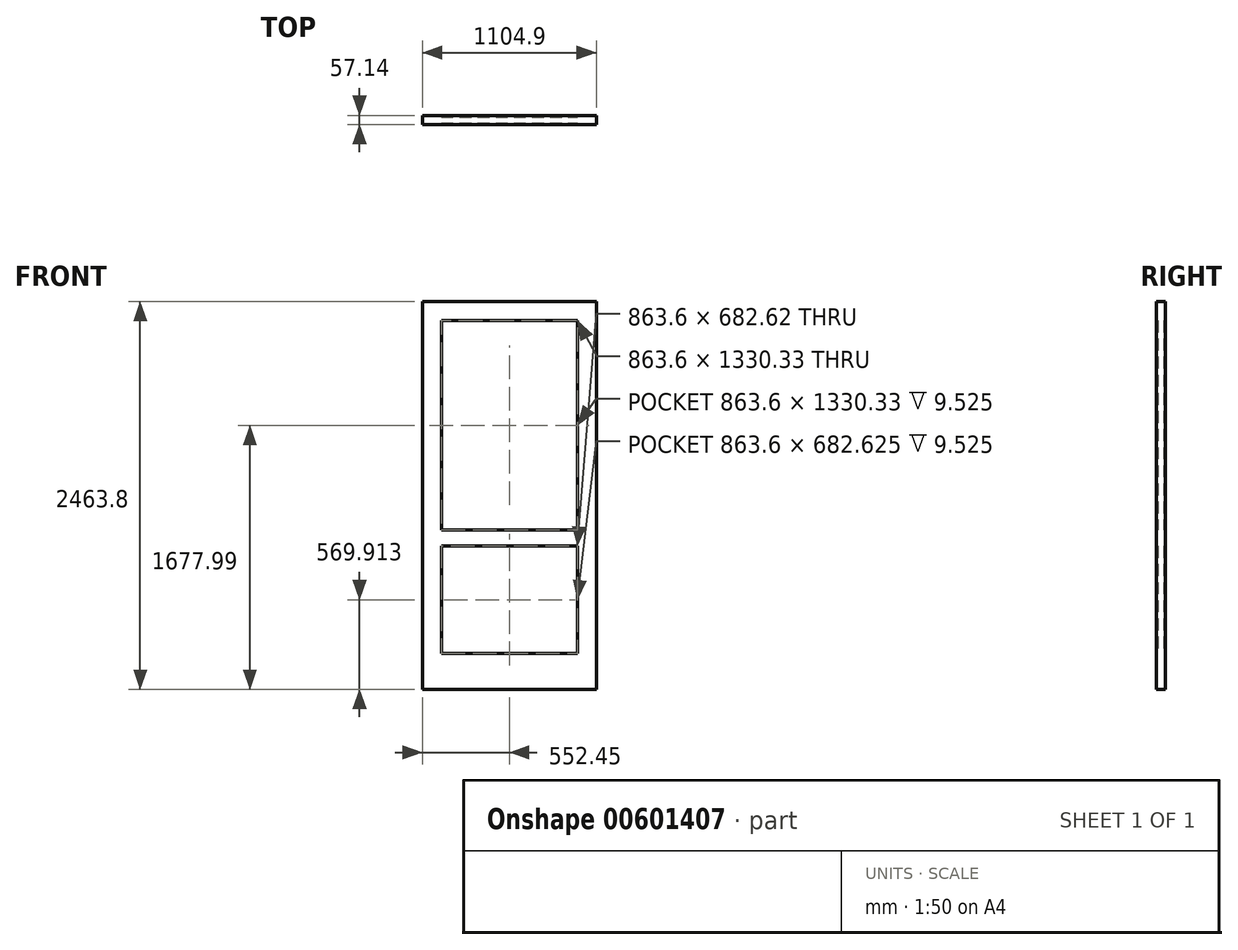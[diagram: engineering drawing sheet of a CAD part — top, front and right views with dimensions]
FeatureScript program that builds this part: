
annotation { "Feature Type Name" : "Feature", "Feature Type Description" : "" }
export const myFeature = defineFeature(function(context is Context, id is Id, definition is map)
    precondition{}
    {
        {
            var Q0;
            Q0=qCreatedBy(makeId("Front.planeOp"),FACE);
            var sketch = newSketch(context, id + "F0", { "sketchPlane" : qUnion([Q0])});
            skLineSegment(sketch, "E0.bottom", {"start": v(0, 0) * mm, "end": v(-1104.9, 0) * mm});
            skLineSegment(sketch, "E0.top", {"start": v(0, 2463.8) * mm, "end": v(-1104.9, 2463.8) * mm});
            skLineSegment(sketch, "E0.left", {"start": v(0, 0) * mm, "end": v(0, 2463.8) * mm});
            skLineSegment(sketch, "E0.right", {"start": v(-1104.9, 0) * mm, "end": v(-1104.9, 2463.8) * mm});
            skLineSegment(sketch, "E1.bottom", {"start": v(-984.25, 2343.15) * mm, "end": v(-120.65, 2343.15) * mm});
            skLineSegment(sketch, "E1.top", {"start": v(-984.25, 228.6) * mm, "end": v(-120.65, 228.6) * mm});
            skLineSegment(sketch, "E1.left", {"start": v(-984.25, 2343.15) * mm, "end": v(-984.25, 228.6) * mm});
            skLineSegment(sketch, "E1.right", {"start": v(-120.65, 2343.15) * mm, "end": v(-120.65, 228.6) * mm});
            skLineSegment(sketch, "E2", {"start": v(-984.25, 911.22) * mm, "end": v(-120.65, 911.23) * mm});
            skLineSegment(sketch, "E3", {"start": v(-984.25, 1012.82) * mm, "end": v(-120.65, 1012.83) * mm});
            skPoint(sketch, "E4.right.end.orphan", {"position": v(-120.65, 1285.88) * mm});
            skLineSegment(sketch, "E5", {"start": v(-120.65, 1012.83) * mm, "end": v(-120.65, 911.23) * mm, "construction": true});
            skLineSegment(sketch, "E6", {"start": v(-984.25, 1012.82) * mm, "end": v(-984.25, 911.22) * mm});
            skLineSegment(sketch, "E7", {"start": v(-120.65, 1012.83) * mm, "end": v(-120.65, 911.23) * mm});
            skSolve(sketch);
        }
        {
            var Q0;
            Q0 = qSketchRegion(id + "F0", true);
            var Q1;
            {var subQ0=sQuery(id+"F0.wireOp",EDGE,"E2");Q1=makeQuery(id+"F0.imprint","IMPRINT",FACE,{"disambiguationData":[TD([[makeQuery(id+"F0.imprint","IMPRINT",EDGE,{"derivedFrom":subQ0}),1.0]])]});}
            extrude(context, id + "F1", {"entities" : qUnion([Q0, Q1]), "endBound" : BoundingType.SYMMETRIC, "depth" : 57.15 * mm, "offsetDistance" : 25.4 * mm});
        }
        {
            var Q0;
            {var subQ0=sQuery(id+"F0.wireOp",EDGE,"E1.bottom");Q0=makeQuery(id+"F0.imprint","IMPRINT",FACE,{"disambiguationData":[TD([[makeQuery(id+"F0.imprint","IMPRINT",EDGE,{"derivedFrom":subQ0}),-1.0]])]});}
            var Q1;
            {var subQ0=sQuery(id+"F0.wireOp",EDGE,"E1.top");Q1=makeQuery(id+"F0.imprint","IMPRINT",FACE,{"disambiguationData":[TD([[makeQuery(id+"F0.imprint","IMPRINT",EDGE,{"derivedFrom":subQ0}),1.0]])]});}
            extrude(context, id + "F2", {"entities" : qUnion([Q0, Q1]), "operationType" : NewBodyOperationType.ADD, "endBound" : BoundingType.SYMMETRIC, "depth" : 38.1 * mm, "offsetDistance" : 25.4 * mm});
        }
    });
